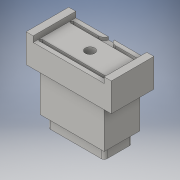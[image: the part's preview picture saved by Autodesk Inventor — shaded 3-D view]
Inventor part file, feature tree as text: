
AUTODESK INVENTOR PART (.ipt)
format: ipt  version: 2016 (Build 200138000, 138)  size: 236,032 bytes
history: native  units: mm
features: sketch x8, extrude x6, projected_geometry x6, fillet x3, hole x2
ambient origin geometry x8: Origin, YZ Plane, XZ Plane, XY Plane, X Axis, Y Axis, Z Axis, Center Point
bodies: Solid1 (feature_tree)
feature tree (25):
  extrude  "Extrusion1"  Depth=30.0mm
  extrude  "Extrusion2"  Depth=10.0mm TaperAngle=0.0deg
  extrude  "Extrusion3"  Depth=2.0mm
  extrude  "Extrusion4"  Depth=19.9mm
  hole  "Hole1"  [1 undecoded]
  fillet  "Fillet1"  Radius=1.0mm
  hole  "Hole3"  [1 undecoded]
  extrude  "Extrusion5"  Depth=2.0mm
  fillet  "Fillet2"  Radius=0.625mm
  extrude  "Extrusion6"  Depth=2.0mm
  fillet  "Fillet3"  Radius=0.625mm
  sketch  "Sketch1"  dims[d0=15.0mm d1=30.0mm]
  sketch  "Sketch2"  dims[d2=10.0mm d3=0.0mm d5=14.0mm d6=0.0mm]
  projected_geometry  "Projected Loop1"
  sketch  "Sketch3"  dims[d7=2.0mm d8=25.0mm]
  projected_geometry  "Projected Loop2"
  sketch  "Sketch4"  dims[d9=15.0mm d10=0.0mm d11=19.9mm]
  projected_geometry  "Projected Loop3"
  sketch  "Sketch5"  dims[d12=9.9mm d13=4.0mm d14=0.0mm]
  sketch  "Sketch7"  dims[d15=3.3mm d16=6.0mm d17=4.0mm d18=2.0mm d19=90.0deg d20=8.0mm d21=20.594885mm d22=1.0mm]
  projected_geometry  "Projected Loop6"
  sketch  "Sketch8"  dims[d32=12.5mm d33=22.5mm]
  projected_geometry  "Projected Loop7"
  sketch  "Sketch9"  dims[d34=0.625mm d35=5.5mm d36=0.625mm d37=5.5mm d38=0.625mm d39=0.625mm d40=5.5mm d41=5.5mm d42=1.0mm d43=6.0mm d44=4.0mm d45=2.0mm d46=90.0deg d47=8.0mm d48=20.594885mm d49=1.0mm d50=0.625mm d51=0.999952mm d52=0.625mm d53=1.0mm d54=0.0mm d55=2.0mm d56=2.0mm d57=1.0mm d58=0.0mm d59=2.0mm]
  projected_geometry  "Projected Loop8"
note: 2 required parameter values undecoded (feature->parameter linkage not recoverable at this tier; creation-order binding heuristic only, values carry confidence <= 0.55)
